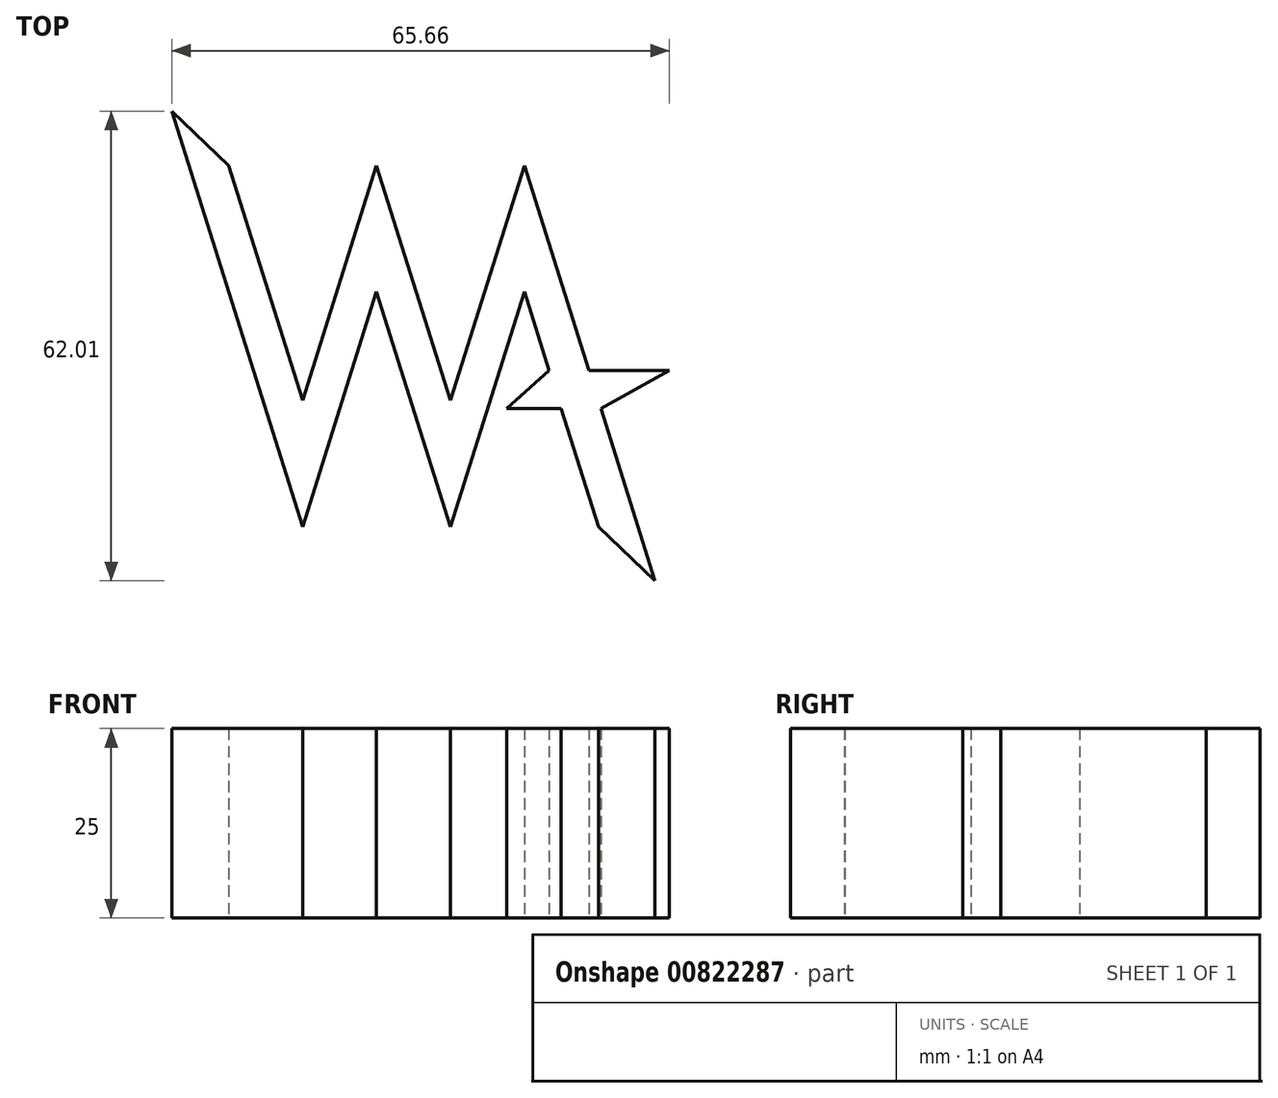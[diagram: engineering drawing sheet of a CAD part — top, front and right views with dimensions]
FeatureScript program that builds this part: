
annotation { "Feature Type Name" : "Feature", "Feature Type Description" : "" }
export const myFeature = defineFeature(function(context is Context, id is Id, definition is map)
    precondition{}
    {
        {
            var Q0;
            Q0=qCreatedBy(makeId("Top.planeOp"),FACE);
            var sketch = newSketch(context, id + "F0", { "sketchPlane" : qUnion([Q0])});
            skLineSegment(sketch, "E0", {"start": v(-62.84, 28.23) * mm, "end": v(-47.84, -19.46) * mm});
            skLineSegment(sketch, "E1", {"start": v(-57.6, 28.23) * mm, "end": v(-47.84, -2.8) * mm});
            skLineSegment(sketch, "E2.MirrorCS", {"start": v(-38.08, 28.23) * mm, "end": v(-47.84, -2.8) * mm});
            skLineSegment(sketch, "E3", {"start": v(-38.08, 28.23) * mm, "end": v(-28.32, -2.8) * mm});
            skLineSegment(sketch, "E4.MirrorCS", {"start": v(-18.56, 28.23) * mm, "end": v(-28.32, -2.8) * mm});
            skLineSegment(sketch, "E5.MirrorCS", {"start": v(-18.56, 11.57) * mm, "end": v(-28.32, -19.46) * mm});
            skPoint(sketch, "E6.start.orphan", {"position": v(-38.08, 43.87) * mm});
            skLineSegment(sketch, "E7", {"start": v(-47.84, -19.46) * mm, "end": v(-38.08, 11.57) * mm});
            skLineSegment(sketch, "E8", {"start": v(-38.08, 11.57) * mm, "end": v(-28.32, -19.46) * mm});
            skLineSegment(sketch, "E9", {"start": v(-18.56, 28.23) * mm, "end": v(-10.04, 1.14) * mm});
            skLineSegment(sketch, "E10", {"start": v(-8.8, -19.5) * mm, "end": v(-13.71, -3.86) * mm});
            skLineSegment(sketch, "E11", {"start": v(-62.84, 28.23) * mm, "end": v(-65.09, 35.39) * mm});
            skLineSegment(sketch, "E12", {"start": v(-65.09, 35.39) * mm, "end": v(-57.6, 28.23) * mm});
            skLineSegment(sketch, "E13", {"start": v(-3.56, -19.46) * mm, "end": v(-1.31, -26.62) * mm});
            skLineSegment(sketch, "E14", {"start": v(-1.31, -26.62) * mm, "end": v(-8.8, -19.5) * mm});
            skLineSegment(sketch, "E15", {"start": v(-10.04, 1.14) * mm, "end": v(-6.93, 1.14) * mm});
            skLineSegment(sketch, "E16", {"start": v(-6.93, 1.14) * mm, "end": v(0.57, 1.14) * mm});
            skLineSegment(sketch, "E17", {"start": v(0.57, 1.14) * mm, "end": v(-8.47, -3.86) * mm});
            skLineSegment(sketch, "E18", {"start": v(-15.29, 1.14) * mm, "end": v(-20.88, -3.86) * mm});
            skLineSegment(sketch, "E19", {"start": v(-20.88, -3.86) * mm, "end": v(-13.71, -3.86) * mm});
            skLineSegment(sketch, "E20.trimOffspring", {"start": v(-15.29, 1.14) * mm, "end": v(-18.56, 11.57) * mm});
            skLineSegment(sketch, "E21.trimOffspring", {"start": v(-8.47, -3.86) * mm, "end": v(-3.56, -19.46) * mm});
            skSolve(sketch);
        }
        {
            var Q0;
            Q0 = qSketchRegion(id + "F0", true);
            extrude(context, id + "F1", {"entities" : qUnion([Q0]), "depth" : 25 * mm, "offsetDistance" : 25 * mm});
        }
    });
